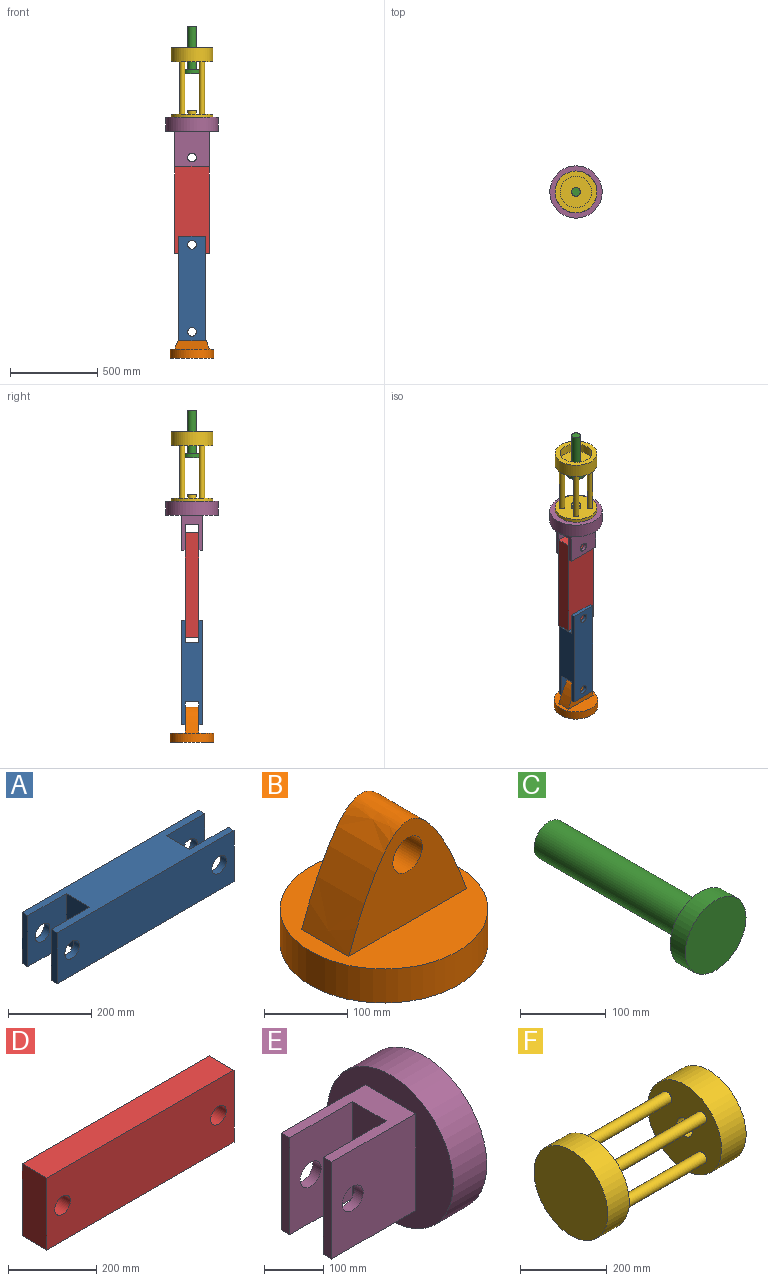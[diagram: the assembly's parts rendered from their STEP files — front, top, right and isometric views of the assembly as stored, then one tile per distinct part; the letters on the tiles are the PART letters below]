
ASSEMBLY  parts=6 mates=5
PART A: 18 faces, bbox 600x120x150 mm
  f0: plane 150x20mm, normal (-1,0,0), area 3000mm2, adj f3,f5,f7,f9
  f1: cylinder r=25mm len=50mm, axis (0,1,0), area 3141.6mm2, adj f7,f9
  f2: plane 150x20mm, normal (-1,0,0), area 3000mm2, adj f3,f5,f6,f10
  f3: plane 600x120mm, normal (0,0,-1), area 51200mm2, adj f0,f2,f6,f7,f8,f9,f10,f11
  f4: cylinder r=25mm len=50mm, axis (0,1,0), area 3141.6mm2, adj f6,f10
  f5: plane 600x120mm, normal (0,0,1), area 51200mm2, adj f0,f2,f6,f7,f8,f9,f10,f11
  f6: plane 600x150mm, normal (0,-1,0), area 86073mm2, adj f2,f3,f4,f5,f13,f14
  f7: plane 600x150mm, normal (0,1,0), area 86073mm2, adj f0,f1,f3,f5,f11,f12
  f8: plane 150x80mm, normal (-1,0,0), area 12000mm2, adj f3,f5,f9,f10
  f9: plane 150x130mm, normal (0,-1,0), area 17536.5mm2, adj f0,f1,f3,f5,f8
  f10: plane 150x130mm, normal (0,1,0), area 17536.5mm2, adj f2,f3,f4,f5,f8
  f11: plane 150x20mm, normal (1,0,0), area 3000mm2, adj f3,f5,f7,f16
  f12: cylinder r=25mm len=50mm, axis (0,1,0), area 3141.6mm2, adj f7,f16
  f13: plane 150x20mm, normal (1,0,0), area 3000mm2, adj f3,f5,f6,f17
  f14: cylinder r=25mm len=50mm, axis (0,1,0), area 3141.6mm2, adj f6,f17
  f15: plane 150x80mm, normal (1,0,0), area 12000mm2, adj f3,f5,f16,f17
  f16: plane 150x130mm, normal (0,-1,0), area 17536.5mm2, adj f3,f5,f11,f12,f15
  f17: plane 150x130mm, normal (0,1,0), area 17536.5mm2, adj f3,f5,f13,f14,f15
PART B: 7 faces, bbox 250x250x209.9 mm
  f0: extruded ~200x150mm, area 29944.2mm2, adj f2,f3,f6
  f1: cylinder r=25mm len=80mm, axis (0,1,0), area 12566.4mm2, adj f2,f3
  f2: plane 200x159.86mm, normal (0,-1,0), area 17567mm2, adj f0,f1,f6
  f3: plane 200x159.86mm, normal (0,1,0), area 17567mm2, adj f0,f1,f6
  f4: cylinder r=125mm len=250mm, axis (0,0,1), area 39269.9mm2, adj f5,f6
  f5: plane 250x250mm, normal (0,0,-1), area 49087.4mm2, adj f4
  f6: plane 250x250mm, normal (0,0,1), area 33087.4mm2, adj f0,f2,f3,f4
PART C: 5 faces, bbox 100x275x100 mm
  f0: cylinder r=25mm len=250mm, axis (0,1,0), area 39269.9mm2, adj f1,f4
  f1: plane 50x50mm, normal (0,1,0), area 1963.5mm2, adj f0
  f2: cylinder r=50mm len=100mm, axis (0,1,0), area 7854mm2, adj f3,f4
  f3: plane 100x100mm, normal (0,-1,0), area 7854mm2, adj f2
  f4: plane 100x100mm, normal (0,1,0), area 5890.5mm2, adj f0,f2
PART D: 8 faces, bbox 600x80x200 mm
  f0: plane 600x80mm, normal (0,0,1), area 48000mm2, adj f1,f4,f5,f6
  f1: plane 200x80mm, normal (-1,0,0), area 16000mm2, adj f0,f2,f4,f5
  f2: plane 600x80mm, normal (0,0,-1), area 48000mm2, adj f1,f4,f5,f6
  f3: cylinder r=25mm len=80mm, axis (0,1,0), area 12566.4mm2, adj f4,f5
  f4: plane 600x200mm, normal (0,-1,0), area 116073mm2, adj f0,f1,f2,f3,f6,f7
  f5: plane 600x200mm, normal (0,1,0), area 116073mm2, adj f0,f1,f2,f3,f6,f7
  f6: plane 200x80mm, normal (1,0,0), area 16000mm2, adj f0,f2,f4,f5
  f7: cylinder r=25mm len=80mm, axis (0,1,0), area 12566.4mm2, adj f4,f5
PART E: 16 faces, bbox 280x300x300 mm
  f0: plane 200x20mm, normal (-1,0,0), area 4000mm2, adj f2,f3,f7,f10
  f1: cylinder r=25mm len=50mm, axis (0,1,0), area 3141.6mm2, adj f7,f10
  f2: plane 200x120mm, normal (0,0,-1), area 12000mm2, adj f0,f5,f6,f7,f8,f9,f10,f13
  f3: plane 200x120mm, normal (0,0,1), area 12000mm2, adj f0,f5,f6,f7,f8,f9,f10,f13
  f4: cylinder r=25mm len=50mm, axis (0,1,0), area 3141.6mm2, adj f6,f9
  f5: plane 200x20mm, normal (-1,0,0), area 4000mm2, adj f2,f3,f6,f9
  f6: plane 200x200mm, normal (0,-1,0), area 38036.5mm2, adj f2,f3,f4,f5,f13
  f7: plane 200x200mm, normal (0,1,0), area 38036.5mm2, adj f0,f1,f2,f3,f13
  f8: plane 200x80mm, normal (-1,0,0), area 16000mm2, adj f2,f3,f9,f10
  f9: plane 200x150mm, normal (0,1,0), area 28036.5mm2, adj f2,f3,f4,f5,f8
  f10: plane 200x150mm, normal (0,-1,0), area 28036.5mm2, adj f0,f1,f2,f3,f8
  f11: cylinder r=150mm len=300mm, axis (-1,0,0), area 75398.2mm2, adj f12,f13
  f12: plane 300x300mm, normal (1,0,0), area 25446.9mm2, adj f11,f14
  f13: plane 300x300mm, normal (-1,0,0), area 46685.8mm2, adj f2,f3,f6,f7,f11
  f14: cylinder r=120mm len=240mm, axis (1,0,0), area 37699.1mm2, adj f12,f15
  f15: plane 240x240mm, normal (1,0,0), area 45238.9mm2, adj f14
PART F: 15 faces, bbox 450x240x240 mm
  f0: cylinder r=120mm len=240mm, axis (-1,0,0), area 52778.8mm2, adj f1,f2
  f1: plane 240x240mm, normal (1,0,0), area 40448mm2, adj f0,f3,f5,f6,f7,f8
  f2: plane 240x240mm, normal (-1,0,0), area 45238.9mm2, adj f0
  f3: cylinder r=25mm len=50mm, axis (-1,0,0), area 3141.6mm2, adj f1,f4
  f4: plane 50x50mm, normal (1,0,0), area 1963.5mm2, adj f3
  f5: cylinder r=15mm len=300mm, axis (-1,0,0), area 28274.3mm2, adj f1,f11
  f6: cylinder r=15mm len=300mm, axis (-1,0,0), area 28274.3mm2, adj f1,f11
  f7: cylinder r=15mm len=300mm, axis (-1,0,0), area 28274.3mm2, adj f1,f11
  f8: cylinder r=15mm len=300mm, axis (-1,0,0), area 28274.3mm2, adj f1,f11
  f9: cylinder r=120mm len=240mm, axis (-1,0,0), area 60318.6mm2, adj f10,f11
  f10: plane 240x240mm, normal (1,0,0), area 19792mm2, adj f9,f12
  f11: plane 240x240mm, normal (-1,0,0), area 40448mm2, adj f5,f6,f7,f8,f9,f14
  f12: cylinder r=90mm len=180mm, axis (1,0,0), area 28274.3mm2, adj f10,f13
  f13: plane 180x180mm, normal (1,0,0), area 23483.4mm2, adj f12,f14
  f14: cylinder r=25mm len=50mm, axis (1,0,0), area 4712.4mm2, adj f11,f13
PLACE A rot(axis=(0,-1,0),90deg) t=(0,0,350)mm
PLACE B at identity fixed
PLACE C rot(axis=(0.58,-0.57,-0.57),119.6deg) t=(63.99,260.26,1730)mm
PLACE D rot(axis=(0,-1,0),90deg) t=(0,0,850)mm
PLACE E rot(axis=(0,-1,0),90deg) t=(0,0,1250)mm
PLACE F rot(axis=(0.01,-1,0.01),90deg) t=(0,0,1280)mm
MATE revolute A.f1 <-> B.f1  axis (0,1,0) through (0,-40,100)mm
MATE revolute D.f7 <-> E.f1  axis (0,1,0) through (0,-40,1100)mm
MATE revolute F.f0 <-> E.f11  axis (0,0,-1) through (0,0,1280)mm
MATE revolute D.f3 <-> A.f12  axis (0,-1,0) through (0,-40,600)mm
MATE slider C.f0 <-> F.f0  axis (0,0,1) through (0,0,1730)mm
